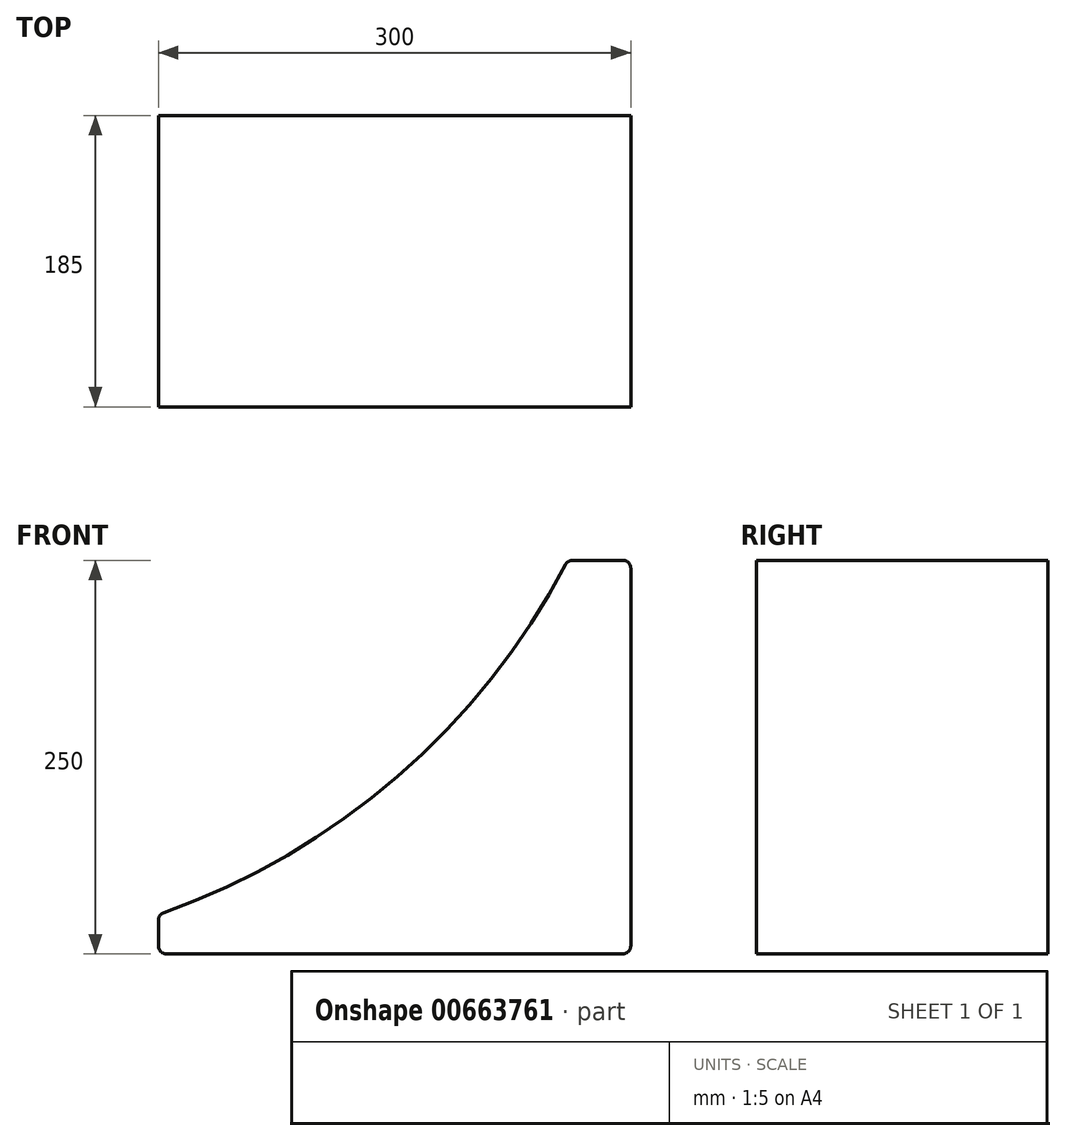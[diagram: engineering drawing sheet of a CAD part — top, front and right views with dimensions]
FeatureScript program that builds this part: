
annotation { "Feature Type Name" : "Feature", "Feature Type Description" : "" }
export const myFeature = defineFeature(function(context is Context, id is Id, definition is map)
    precondition{}
    {
        {
            var Q0;
            Q0=qCreatedBy(makeId("Front.planeOp"), FACE);
            var sketch = newSketch(context, id + "F0", { "sketchPlane" : qUnion([Q0])});
            skLineSegment(sketch, "E0.bottom", {"start": v(-145, -157.14) * mm, "end": v(145, -157.14) * mm});
            skLineSegment(sketch, "E0.right", {"start": v(150, -152.14) * mm, "end": v(150, 87.86) * mm});
            skPoint(sketch, "E0.middle", {"position": v(0, 0) * mm});
            skLineSegment(sketch, "E1", {"start": v(-150, -135.69) * mm, "end": v(-150, -152.14) * mm});
            skArc(sketch, "E2", {"start": v(-146.67, -130.98) * mm, "mid": v(1.8, -44.45) * mm, "end": v(108.6, 90.19) * mm});
            skLineSegment(sketch, "E3", {"start": v(113.03, 92.86) * mm, "end": v(145, 92.86) * mm});
            skPoint(sketch, "E4.visualSharp", {"position": v(110, 92.86) * mm});
            skArc(sketch, "E4.filletArc", {"start": v(113.03, 92.86) * mm, "mid": v(110.45, 92.14) * mm, "end": v(108.6, 90.19) * mm});
            skPoint(sketch, "E5.visualSharp", {"position": v(150, 92.86) * mm});
            skArc(sketch, "E5.filletArc", {"start": v(150, 87.86) * mm, "mid": v(148.54, 91.4) * mm, "end": v(145, 92.86) * mm});
            skPoint(sketch, "E6.visualSharp", {"position": v(-150, -132.14) * mm});
            skArc(sketch, "E6.filletArc", {"start": v(-146.67, -130.98) * mm, "mid": v(-149.08, -132.8) * mm, "end": v(-150, -135.69) * mm});
            skPoint(sketch, "E7.visualSharp", {"position": v(-150, -157.14) * mm});
            skArc(sketch, "E7.filletArc", {"start": v(-150, -152.14) * mm, "mid": v(-148.54, -155.68) * mm, "end": v(-145, -157.14) * mm});
            skPoint(sketch, "E8.visualSharp", {"position": v(150, -157.14) * mm});
            skArc(sketch, "E8.filletArc", {"start": v(145, -157.14) * mm, "mid": v(148.54, -155.68) * mm, "end": v(150, -152.14) * mm});
            skSolve(sketch);
        }
        {
            var Q0;
            Q0 = qSketchRegion(id + "F0", true);
            extrude(context, id + "F1", {"entities" : qUnion([Q0]), "depth" : 185 * mm, "offsetDistance" : 25 * mm});
        }
    });
